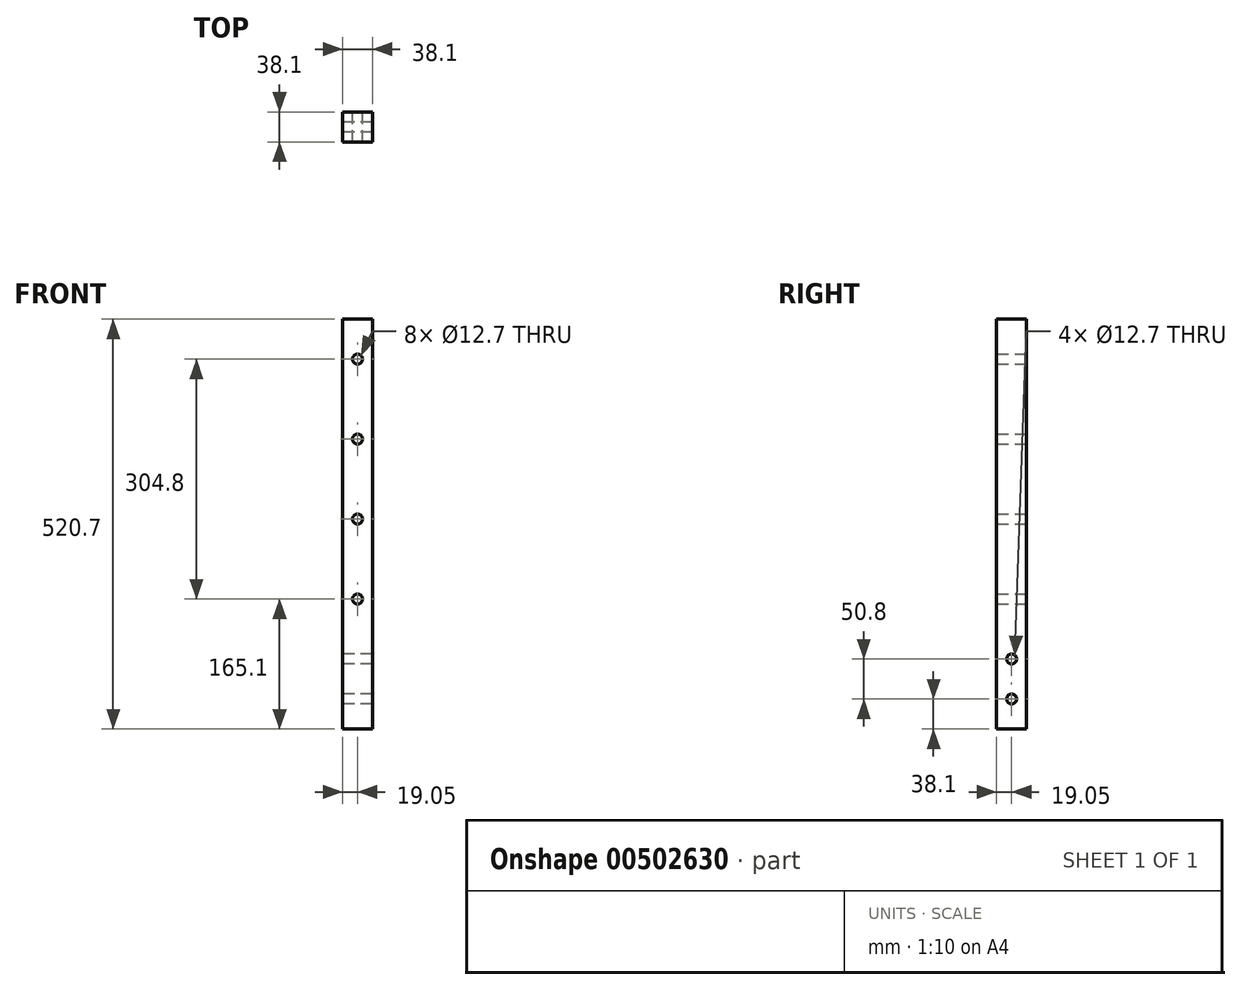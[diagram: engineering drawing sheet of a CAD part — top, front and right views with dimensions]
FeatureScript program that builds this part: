
annotation { "Feature Type Name" : "Feature", "Feature Type Description" : "" }
export const myFeature = defineFeature(function(context is Context, id is Id, definition is map)
    precondition{}
    {
        {
            var Q0;
            Q0=qCreatedBy(makeId("Front.planeOp"),FACE);
            var sketch = newSketch(context, id + "F0", { "sketchPlane" : qUnion([Q0])});
            skLineSegment(sketch, "E0.bottom", {"start": v(0, 0) * mm, "end": v(38.1, 0) * mm});
            skLineSegment(sketch, "E0.top", {"start": v(0, 520.7) * mm, "end": v(38.1, 520.7) * mm});
            skLineSegment(sketch, "E0.left", {"start": v(0, 0) * mm, "end": v(0, 520.7) * mm});
            skLineSegment(sketch, "E0.right", {"start": v(38.1, 0) * mm, "end": v(38.1, 520.7) * mm});
            skCircle(sketch, "E1", {"center": v(19.05, 165.1) * mm, "radius": 6.35 * mm});
            skCircle(sketch, "E2", {"center": v(19.05, 266.7) * mm, "radius": 6.35 * mm});
            skCircle(sketch, "E3", {"center": v(19.05, 368.3) * mm, "radius": 6.35 * mm});
            skCircle(sketch, "E4", {"center": v(19.05, 469.9) * mm, "radius": 6.35 * mm});
            skSolve(sketch);
        }
        {
            var Q0;
            Q0=makeQuery(id+"F0.imprint","IMPRINT",FACE,{"disambiguationData":[TD([[makeQuery(id+"F0.imprint","IMPRINT",EDGE,{"derivedFrom":sQuery(id+"F0.wireOp",EDGE,"E0.bottom")}),1.0]])]});
            extrude(context, id + "F1", {"entities" : qUnion([Q0]), "depth" : 38.1 * mm});
        }
        {
            var Q0;
            Q0=makeQuery(id+"F1.opExtrude","SWEPT_FACE",FACE,{"disambiguationData":[OSD([sQuery(id+"F0.wireOp",EDGE,"E0.left")])]});
            var sketch = newSketch(context, id + "F2", { "sketchPlane" : qUnion([Q0])});
            skCircle(sketch, "E5", {"center": v(19.05, 38.1) * mm, "radius": 6.35 * mm});
            skCircle(sketch, "E6", {"center": v(19.05, 88.9) * mm, "radius": 6.35 * mm});
            skSolve(sketch);
        }
        {
            var Q0;
            Q0=makeQuery(id+"F2.imprint","IMPRINT",FACE,{"disambiguationData":[TD([[makeQuery(id+"F2.imprint","IMPRINT",EDGE,{"derivedFrom":sQuery(id+"F2.wireOp",EDGE,"E5")}),1.0]])]});
            var Q1;
            Q1=makeQuery(id+"F2.imprint","IMPRINT",FACE,{"disambiguationData":[TD([[makeQuery(id+"F2.imprint","IMPRINT",EDGE,{"derivedFrom":sQuery(id+"F2.wireOp",EDGE,"E6")}),1.0]])]});
            extrude(context, id + "F3", {"entities" : qUnion([Q0, Q1]), "operationType" : NewBodyOperationType.REMOVE, "endBound" : BoundingType.THROUGH_ALL, "oppositeDirection" : true, "depth" : 25.4 * mm});
        }
    });
